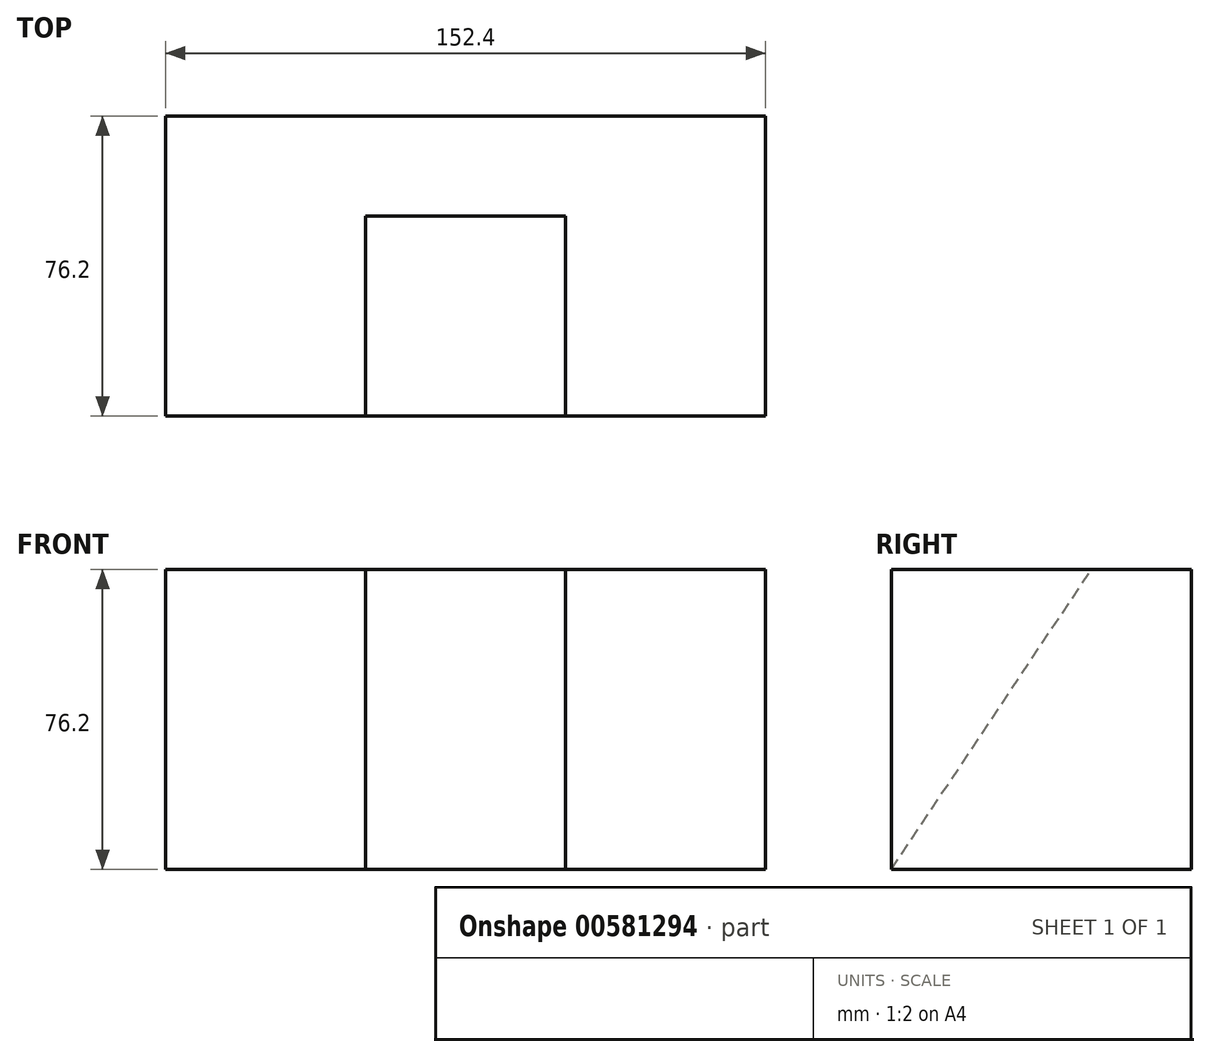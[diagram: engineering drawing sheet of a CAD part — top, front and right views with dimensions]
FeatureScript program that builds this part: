
annotation { "Feature Type Name" : "Feature", "Feature Type Description" : "" }
export const myFeature = defineFeature(function(context is Context, id is Id, definition is map)
    precondition{}
    {
        {
            var Q0;
            Q0=qCreatedBy(makeId("Top.planeOp"),FACE);
            var sketch = newSketch(context, id + "F0", { "sketchPlane" : qUnion([Q0])});
            skLineSegment(sketch, "E0.bottom", {"start": v(-79.22, 15.96) * mm, "end": v(73.18, 15.96) * mm});
            skLineSegment(sketch, "E0.top", {"start": v(-79.22, -60.24) * mm, "end": v(73.18, -60.24) * mm});
            skLineSegment(sketch, "E0.left", {"start": v(-79.22, 15.96) * mm, "end": v(-79.22, -60.24) * mm});
            skLineSegment(sketch, "E0.right", {"start": v(73.18, 15.96) * mm, "end": v(73.18, -60.24) * mm});
            skSolve(sketch);
        }
        {
            var Q0;
            Q0=qSketchRegion(id+"F0",true);
            extrude(context, id + "F1", {"entities" : qUnion([Q0]), "depth" : 101.6 * mm, "offsetDistance" : 25.4 * mm});
        }
        {
            var Q0;
            Q0=makeQuery(id+"F1.opExtrude","SWEPT_FACE",FACE,{"disambiguationData":[OSD([sQuery(id+"F0.wireOp",EDGE,"E0.right")])]});
            var sketch = newSketch(context, id + "F2", { "sketchPlane" : qUnion([Q0])});
            skLineSegment(sketch, "E1.bottom", {"start": v(-60.24, 0) * mm, "end": v(15.96, 0) * mm});
            skLineSegment(sketch, "E1.top", {"start": v(-60.24, 76.2) * mm, "end": v(15.96, 76.2) * mm});
            skLineSegment(sketch, "E1.left", {"start": v(-60.24, 0) * mm, "end": v(-60.24, 76.2) * mm});
            skLineSegment(sketch, "E1.right", {"start": v(15.96, 0) * mm, "end": v(15.96, 76.2) * mm});
            skLineSegment(sketch, "E2.bottom", {"start": v(15.96, 76.2) * mm, "end": v(-9.44, 76.2) * mm});
            skLineSegment(sketch, "E2.top", {"start": v(15.96, 101.6) * mm, "end": v(-9.44, 101.6) * mm});
            skLineSegment(sketch, "E2.left", {"start": v(15.96, 76.2) * mm, "end": v(15.96, 101.6) * mm});
            skLineSegment(sketch, "E2.right", {"start": v(-9.44, 76.2) * mm, "end": v(-9.44, 101.6) * mm});
            skSolve(sketch);
        }
        {
            var Q0;
            {var subQ0=sQuery(id+"F2.wireOp",EDGE,"E1.top");Q0=makeQuery(id+"F2.imprint","IMPRINT",FACE,{"disambiguationData":[TD([[makeQuery(id+"F2.imprint","IMPRINT",EDGE,{"derivedFrom":subQ0}),1.0]])]});}
            extrude(context, id + "F3", {"entities" : qUnion([Q0]), "operationType" : NewBodyOperationType.REMOVE, "oppositeDirection" : true, "depth" : 152.4 * mm, "offsetDistance" : 25.4 * mm});
        }
        {
            var Q0;
            Q0=makeQuery(id+"F1.opExtrude","SWEPT_FACE",FACE,{"disambiguationData":[OSD([sQuery(id+"F0.wireOp",EDGE,"E0.top")])]});
            var sketch = newSketch(context, id + "F4", { "sketchPlane" : qUnion([Q0])});
            skLineSegment(sketch, "E3.bottom", {"start": v(-79.22, 76.2) * mm, "end": v(-28.42, 76.2) * mm});
            skLineSegment(sketch, "E3.top", {"start": v(-79.22, 0) * mm, "end": v(-28.42, 0) * mm});
            skLineSegment(sketch, "E3.left", {"start": v(-79.22, 76.2) * mm, "end": v(-79.22, 0) * mm});
            skLineSegment(sketch, "E3.right", {"start": v(-28.42, 76.2) * mm, "end": v(-28.42, 0) * mm});
            skLineSegment(sketch, "E4.bottom", {"start": v(73.18, 76.2) * mm, "end": v(22.38, 76.2) * mm});
            skLineSegment(sketch, "E4.top", {"start": v(73.18, 0) * mm, "end": v(22.38, 0) * mm});
            skLineSegment(sketch, "E4.left", {"start": v(73.18, 76.2) * mm, "end": v(73.18, 0) * mm});
            skLineSegment(sketch, "E4.right", {"start": v(22.38, 76.2) * mm, "end": v(22.38, 0) * mm});
            skSolve(sketch);
        }
        {
            var Q0;
            {var subQ0=sQuery(id+"F4.wireOp",EDGE,"E3.right");Q0=makeQuery(id+"F4.imprint","IMPRINT",FACE,{"disambiguationData":[TD([[makeQuery(id+"F4.imprint","IMPRINT",EDGE,{"derivedFrom":subQ0}),1.0]])]});}
            extrude(context, id + "F5", {"entities" : qUnion([Q0]), "operationType" : NewBodyOperationType.REMOVE, "oppositeDirection" : true, "depth" : 50.8 * mm, "offsetDistance" : 25.4 * mm});
        }
        {
            var Q0;
            Q0=makeQuery(id+"F5.boolean.opBoolean","COPY",FACE,{"derivedFrom":makeQuery(id+"F5.opExtrude","SWEPT_FACE",FACE,{"disambiguationData":[OSD([sQuery(id+"F4.wireOp",EDGE,"E3.right")])]})});
            var sketch = newSketch(context, id + "F6", { "sketchPlane" : qUnion([Q0])});
            skLineSegment(sketch, "E5.bottom", {"start": v(-60.24, 76.2) * mm, "end": v(-9.44, 76.2) * mm});
            skLineSegment(sketch, "E5.top", {"start": v(-60.24, 0) * mm, "end": v(-9.44, 0) * mm});
            skLineSegment(sketch, "E5.left", {"start": v(-60.24, 76.2) * mm, "end": v(-60.24, 0) * mm});
            skLineSegment(sketch, "E5.right", {"start": v(-9.44, 76.2) * mm, "end": v(-9.44, 0) * mm});
            skLineSegment(sketch, "E6", {"start": v(-60.24, 0) * mm, "end": v(-9.44, 76.2) * mm});
            skSolve(sketch);
        }
        {
            var Q0;
            Q0=makeQuery(id+"F6.imprint","IMPRINT",FACE,{"disambiguationData":[TD([[makeQuery(id+"F6.imprint","IMPRINT",EDGE,{"derivedFrom":sQuery(id+"F6.wireOp",EDGE,"E5.top")}),-1.0]])]});
            extrude(context, id + "F7", {"entities" : qUnion([Q0]), "operationType" : NewBodyOperationType.ADD, "depth" : 50.8 * mm, "offsetDistance" : 25.4 * mm});
        }
    });
